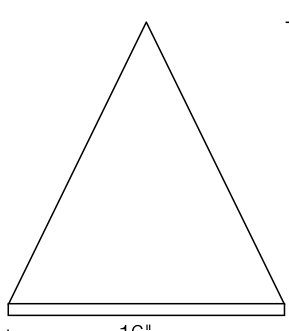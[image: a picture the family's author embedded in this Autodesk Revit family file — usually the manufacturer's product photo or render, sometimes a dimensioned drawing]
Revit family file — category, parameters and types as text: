
# Revit family: M2WDXA
name_source: partatom
category: Lighting Fixtures
units: mm (PartAtom-declared; Revit-internal decimal feet)

## family parameters
Cut with Voids When Loaded = No
Host = Face
Light Source = Yes
OmniClass Number = 23.80.70.14.14
OmniClass Title = Exterior Floodlights
Part Type = Normal
Room Calculation Point = No
Round Connector Dimension = Use Diameter
Shared = Yes

## types (21) — shared parameters
Apparent Load = 0 VA
Color Filter = 16777215
Default Elevation = 48 "
Description = Horizontal reflector downlight with extended arm
Dimming Lamp Color Temperature Shift = <None>
Finish = Die Cast Aluminium
Finish 2 = Silicon Gasket
Glass = Glass
Lamp = One
Manufacturer = Architectural Area Lighting
Model = M2WDXA
Tilt Angle = 90.00°
Wattage Comments = 57 and 70 watts High Output Fluorescent

## per-type parameters (varying)
| type | Photometric Web File | URL |
| M2WDXA-T2-32LED-3K-700 | M2-T2-32LED-3K-700.ies | https://www.currentlighting.com |
| M2WDXA-T3-32LED-3K-700 | M2-T3-32LED-3K-700.ies | https://www.currentlighting.com |
| M2WDXA-T4-32LED-3K-700 | M2-T4-32LED-3K-700.ies | https://www.currentlighting.com |
| M2WDXA-T4-32LED-3K-HSS-700 | M2-T4-32LED-3K-HSS-700.ies | https://www.currentlighting.com |
| M2WDXA-T5-32LED-3K-700 | M2-T5-32LED-3K-700.ies | https://www.currentlighting.com |
| M2WDXA-TL-32LED-3K-700 | M2-TL-32LED-3K-700.ies | https://www.currentlighting.com |
| M2WDXA-TR-32LED-3K-700 | M2-TR-32LED-3K-700.ies | https://www.currentlighting.com |
| M2WDXA-T2-32LED-4K-700 | M2-T2-32LED-4K-700.ies | https://www.currentlighting.com |
| M2WDXA-T3-32LED-4K-700 | M2-T3-32LED-4K-700.ies | https://www.currentlighting.com |
| M2WDXA-T4-32LED-4K-700 | M2-T4-32LED-4K-700.ies | https://www.currentlighting.com |
| M2WDXA-T4-32LED-4K-HSS-700 | M2-T4-32LED-4K-HSS-700.ies | https://www.currentlighting.com |
| M2WDXA-T5-32LED-4K-700 | M2-T5-32LED-4K-700.ies | https://www.currentlighting.com |
| M2WDXA-TL-32LED-4K-700 | M2-TL-32LED-4K-700.ies | http://www.aal.net |
| M2WDXA-T2-32LED-5K-700 | M2-T2-32LED-5K-700.ies | https://www.currentlighting.com |
| M2WDXA-T2-32LED-5K-HSS-700 | M2-T2-32LED-5K-HSS-700.ies | https://www.currentlighting.com |
| M2WDXA-T3-32LED-5K-700 | M2-T3-32LED-5K-700.ies | https://www.currentlighting.com |
| M2WDXA-T4-32LED-5K-700 | M2-T4-32LED-5K-700.ies | https://www.currentlighting.com |
| M2WDXA-T4-32LED-5K-HSS-700 | M2-T4-32LED-5K-HSS-700.ies | https://www.currentlighting.com |
| M2WDXA-T5-32LED-5K-700 | M2-T5-32LED-5K-700.ies | https://www.currentlighting.com |
| M2WDXA-TL-32LED-5K-700 | M2-TL-32LED-5K-700.ies | https://www.currentlighting.com |
| M2WDXA-TR-32LED-5K-700 | M2-TR-32LED-5K-700.ies | https://www.currentlighting.com |

## geometry (parser evidence)
native form markers: Blend x11, Sweep x4
no freeform markers — native parametric forms only
